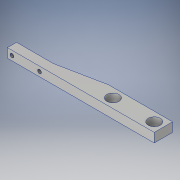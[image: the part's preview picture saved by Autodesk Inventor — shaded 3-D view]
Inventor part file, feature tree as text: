
AUTODESK INVENTOR PART (.ipt)
format: ipt  version: 2017 (Build 210142000, 142)  size: 113,664 bytes
history: native  units: in
note: dims shown in document units (in); Inventor stores cm internally (conversion verified against a paired STEP export)
features: other x3, sketch x3
ambient origin geometry x8: Origin, YZ Plane, XZ Plane, XY Plane, X Axis, Y Axis, Z Axis, Center Point
bodies: Solid1 (feature_tree)
feature tree (6):
  other  "WheelSuspensionFork.ipt"
  other  "Solid1::WheelSuspensionFork.ipt"
  other  "TaggingFeature1"
  sketch  "Sketch1"  dims[d0=0.3937in]
  sketch  "Sketch5"
  sketch  "Sketch6"
